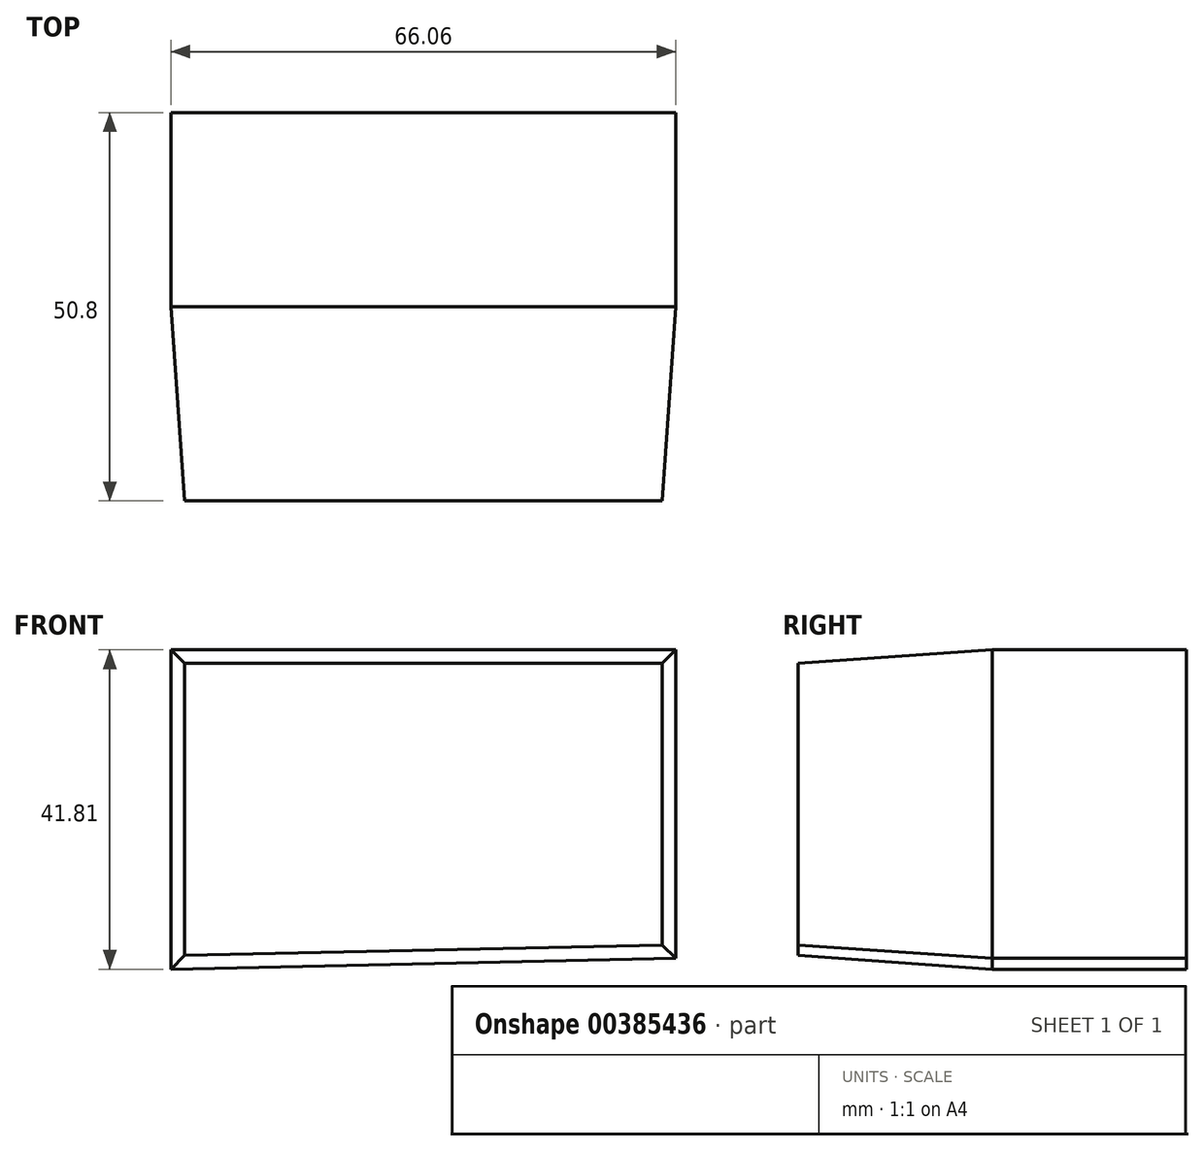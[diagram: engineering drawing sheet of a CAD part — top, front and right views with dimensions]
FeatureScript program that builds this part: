
annotation { "Feature Type Name" : "Feature", "Feature Type Description" : "" }
export const myFeature = defineFeature(function(context is Context, id is Id, definition is map)
    precondition{}
    {
        {
            var Q0;
            Q0=qCreatedBy(makeId("Front.planeOp"),FACE);
            var sketch = newSketch(context, id + "F0", { "sketchPlane" : qUnion([Q0])});
            skLineSegment(sketch, "E0", {"start": v(0, -41.8) * mm, "end": v(0, 0) * mm});
            skLineSegment(sketch, "E1", {"start": v(0, 0) * mm, "end": v(66.06, 0) * mm});
            skLineSegment(sketch, "E2", {"start": v(66.06, 0) * mm, "end": v(66.06, -40.4) * mm});
            skLineSegment(sketch, "E3", {"start": v(66.06, -40.4) * mm, "end": v(0, -41.8) * mm});
            skSolve(sketch);
        }
        {
            var Q0;
            Q0 = qSketchRegion(id + "F0", true);
            extrude(context, id + "F1", {"entities" : qUnion([Q0]), "depth" : 25.4 * mm, "hasDraft" : true, "draftAngle" : 4 * degree, "draftPullDirection" : true, "hasSecondDirection" : true, "secondDirectionOppositeDirection" : true, "secondDirectionDepth" : 25.4 * mm});
        }
    });
